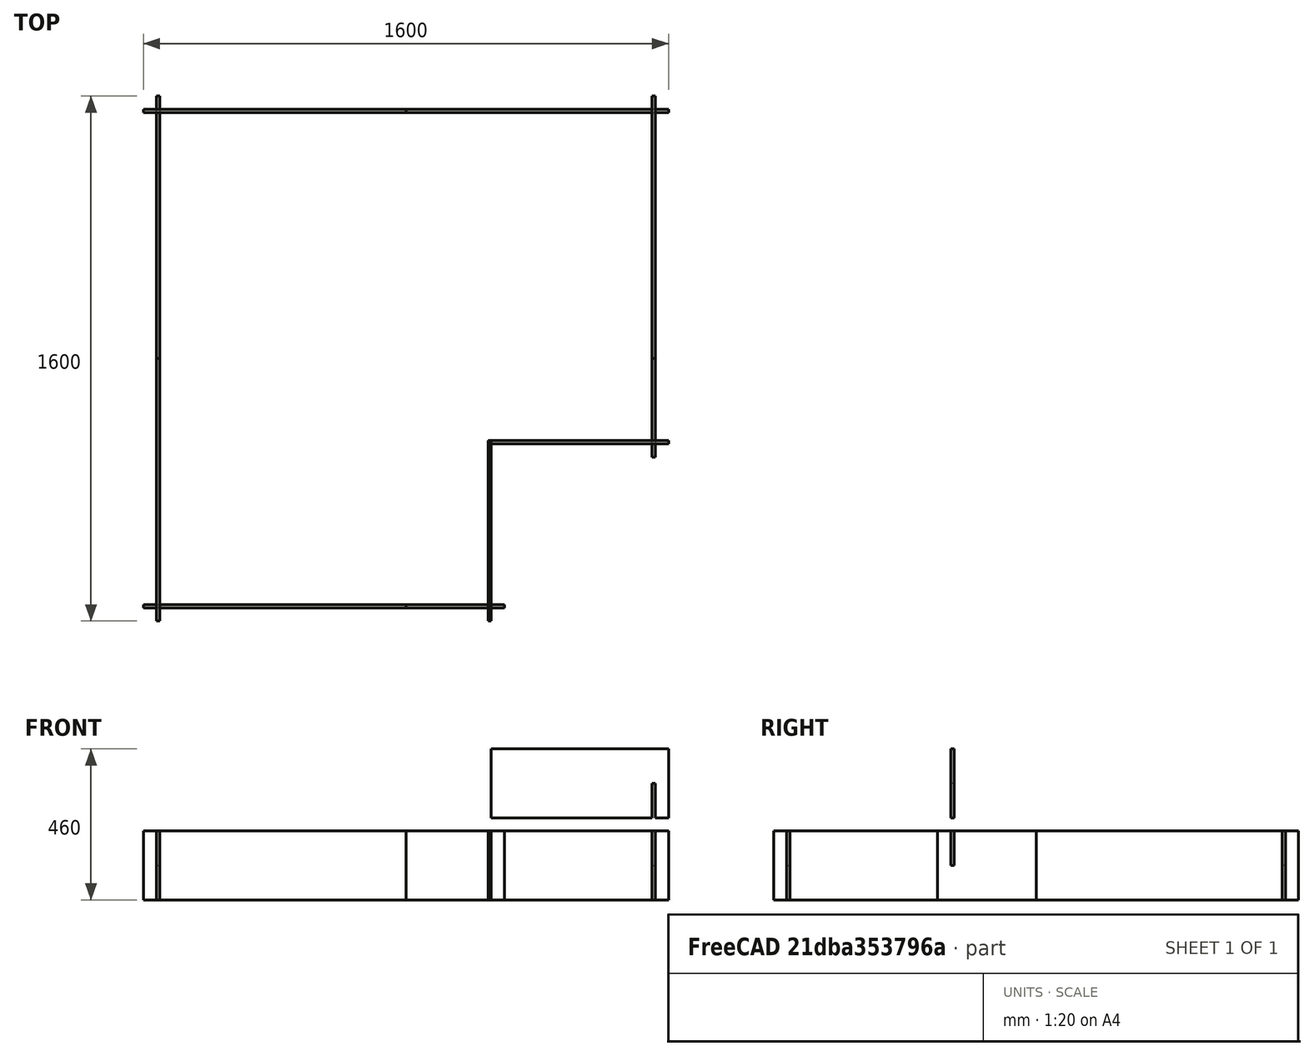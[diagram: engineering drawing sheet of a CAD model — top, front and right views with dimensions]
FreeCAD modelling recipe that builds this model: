
FCSTD DOCUMENT  (FreeCAD 0.21R30769 (Git))
Label: simpler-arena
License: All rights reserved
LicenseURL: http://en.wikipedia.org/wiki/All_rights_reserved
objects: TechDraw::DrawViewAnnotation×14, TechDraw::DrawViewDimension×12, PartDesign::ShapeBinder×11, PartDesign::Body×11, PartDesign::Pad×10, PartDesign::Pocket×10, PartDesign::SubShapeBinder×9, Sketcher::SketchObject×6, TechDraw::DrawViewPart×6, TechDraw::DrawHatch×5, TechDraw::DrawSVGTemplate×3, TechDraw::DrawPage×3, Spreadsheet::Sheet×2, App::Part×2, TechDraw::DrawLeaderLine×1
note: 77 computed .brp shape members not serialized (recipe doc carries the construction recipe); baked Part::Feature solids carry a one-line shape summary decoded from their .brp

FEATURE [Sketcher::SketchObject] Sketch  label="MainSketch"
  FullyConstrained = true
  MapMode = 5
  Support = -> [XY_Plane001]
  expr: Constraints[13] = Spreadsheet.arena_cutout_width
  expr: Constraints[14] = Spreadsheet.arena_inner_width
  expr: Constraints[15] = Spreadsheet.arena_inner_height
  expr: Constraints[16] = Spreadsheet.arena_cutout_height
  sketch-geometry (6):
    g0: LineSegment StartX=-750 StartY=750 StartZ=0 EndX=750 EndY=750 EndZ=0
    g1: LineSegment StartX=750 StartY=750 StartZ=0 EndX=750 EndY=-250 EndZ=0
    g2: LineSegment StartX=250 StartY=-750 StartZ=0 EndX=-750 EndY=-750 EndZ=0
    g3: LineSegment StartX=-750 StartY=-750 StartZ=0 EndX=-750 EndY=750 EndZ=0
    g4: LineSegment StartX=250 StartY=-750 StartZ=0 EndX=250 EndY=-250 EndZ=0
    g5: LineSegment StartX=250 StartY=-250 StartZ=0 EndX=750 EndY=-250 EndZ=0
  constraints (17):
    c: Coincident(g0,g1)
    c: Coincident(g2,g3)
    c: Coincident(g3,g0)
    c: Horizontal(g0)
    c: Horizontal(g2)
    c: Vertical(g1)
    c: Vertical(g3)
    c: Vertical(g4)
    c: Coincident(g5,g4)
    c: Horizontal(g5)
    c: Coincident(g1,g5)
    c: Coincident(g2,g4)
    c: Symmetric(g0,g2,g-1)
    c: DistanceX(g5,g5) = 500
    c: DistanceX(g0,g0) = 1500
    c: DistanceY(g3,g3) = 1500
    c: DistanceY(g4,g4) = 500
FEATURE [Sketcher::SketchObject] Sketch001  label="WallSketch"
  ExternalGeometry = -> [Sketch]
  FullyConstrained = true
  MapMode = 5
  Support = -> [XY_Plane001]
  expr: .Constraints.tab = Spreadsheet.tab_length
  expr: Constraints[101] = Spreadsheet.tab_length
  expr: Constraints[102] = Spreadsheet.tab_length
  expr: Constraints[103] = Spreadsheet.tab_length
  expr: Constraints[109] = Spreadsheet.tab_length
  expr: Constraints[91] = Spreadsheet.wall_thickness
  sketch-geometry (40):
    g0: LineSegment StartX=-750 StartY=0 StartZ=0 EndX=-760 EndY=0 EndZ=0
    g1: LineSegment StartX=-760 StartY=0 StartZ=0 EndX=-760 EndY=800 EndZ=0
    g2: LineSegment StartX=-760 StartY=800 StartZ=0 EndX=-750 EndY=800 EndZ=0
    g3: LineSegment StartX=-750 StartY=800 StartZ=0 EndX=-750 EndY=0 EndZ=0
    g4: LineSegment StartX=-750 StartY=0 StartZ=0 EndX=-760 EndY=0 EndZ=0
    g5: LineSegment StartX=-760 StartY=0 StartZ=0 EndX=-760 EndY=-800 EndZ=0
    g6: LineSegment StartX=-760 StartY=-800 StartZ=0 EndX=-750 EndY=-800 EndZ=0
    g7: LineSegment StartX=-750 StartY=-800 StartZ=0 EndX=-750 EndY=0 EndZ=0
    g8: LineSegment StartX=0 StartY=-750 StartZ=0 EndX=-800 EndY=-750 EndZ=0
    g9: LineSegment StartX=-800 StartY=-750 StartZ=0 EndX=-800 EndY=-760 EndZ=0
    g10: LineSegment StartX=-800 StartY=-760 StartZ=0 EndX=0 EndY=-760 EndZ=0
    g11: LineSegment StartX=0 StartY=-760 StartZ=0 EndX=0 EndY=-750 EndZ=0
    g12: LineSegment StartX=0 StartY=-750 StartZ=0 EndX=300 EndY=-750 EndZ=0
    g13: LineSegment StartX=300 StartY=-750 StartZ=0 EndX=300 EndY=-760 EndZ=0
    g14: LineSegment StartX=300 StartY=-760 StartZ=0 EndX=0 EndY=-760 EndZ=0
    g15: LineSegment StartX=0 StartY=-760 StartZ=0 EndX=0 EndY=-750 EndZ=0
    g16: LineSegment StartX=250 StartY=-250 StartZ=0 EndX=260 EndY=-250 EndZ=0
    g17: LineSegment StartX=260 StartY=-250 StartZ=0 EndX=260 EndY=-800 EndZ=0
    g18: LineSegment StartX=260 StartY=-800 StartZ=0 EndX=250 EndY=-800 EndZ=0
    g19: LineSegment StartX=250 StartY=-800 StartZ=0 EndX=250 EndY=-250 EndZ=0
    g20: LineSegment StartX=260 StartY=-250 StartZ=0 EndX=800 EndY=-250 EndZ=0
    g21: LineSegment StartX=800 StartY=-250 StartZ=0 EndX=800 EndY=-260 EndZ=0
    g22: LineSegment StartX=800 StartY=-260 StartZ=0 EndX=260 EndY=-260 EndZ=0
    g23: LineSegment StartX=260 StartY=-260 StartZ=0 EndX=260 EndY=-250 EndZ=0
    g24: LineSegment StartX=750 StartY=0 StartZ=0 EndX=760 EndY=0 EndZ=0
    g25: LineSegment StartX=760 StartY=0 StartZ=0 EndX=760 EndY=-300 EndZ=0
    g26: LineSegment StartX=760 StartY=-300 StartZ=0 EndX=750 EndY=-300 EndZ=0
    g27: LineSegment StartX=750 StartY=-300 StartZ=0 EndX=750 EndY=0 EndZ=0
    g28: LineSegment StartX=750 StartY=0 StartZ=0 EndX=760 EndY=0 EndZ=0
    g29: LineSegment StartX=760 StartY=0 StartZ=0 EndX=760 EndY=800 EndZ=0
    g30: LineSegment StartX=760 StartY=800 StartZ=0 EndX=750 EndY=800 EndZ=0
    g31: LineSegment StartX=750 StartY=800 StartZ=0 EndX=750 EndY=0 EndZ=0
    g32: LineSegment StartX=0 StartY=750 StartZ=0 EndX=800 EndY=750 EndZ=0
    g33: LineSegment StartX=800 StartY=750 StartZ=0 EndX=800 EndY=760 EndZ=0
    g34: LineSegment StartX=800 StartY=760 StartZ=0 EndX=0 EndY=760 EndZ=0
    g35: LineSegment StartX=0 StartY=760 StartZ=0 EndX=0 EndY=750 EndZ=0
    g36: LineSegment StartX=0 StartY=750 StartZ=0 EndX=-800 EndY=750 EndZ=0
    g37: LineSegment StartX=-800 StartY=750 StartZ=0 EndX=-800 EndY=760 EndZ=0
    g38: LineSegment StartX=-800 StartY=760 StartZ=0 EndX=0 EndY=760 EndZ=0
    g39: LineSegment StartX=0 StartY=760 StartZ=0 EndX=0 EndY=750 EndZ=0
  constraints (114):
    c: Coincident(g0,g1)
    c: Coincident(g1,g2)
    c: Coincident(g2,g3)
    c: Coincident(g3,g0)
    c: Horizontal(g0)
    c: Horizontal(g2)
    c: Vertical(g1)
    c: Vertical(g3)
    c: PointOnObject(g0,g-4)
    c: Coincident(g4,g5)
    c: Coincident(g5,g6)
    c: Coincident(g6,g7)
    c: Coincident(g7,g4)
    c: Horizontal(g4)
    c: Horizontal(g6)
    c: Vertical(g5)
    c: Vertical(g7)
    c: PointOnObject(g4,g-4)
    c: Coincident(g8,g9)
    c: Coincident(g9,g10)
    c: Coincident(g10,g11)
    c: Coincident(g11,g8)
    c: Horizontal(g8)
    c: Horizontal(g10)
    c: Vertical(g9)
    c: Vertical(g11)
    c: PointOnObject(g8,g-5)
    c: Coincident(g12,g13)
    c: Coincident(g13,g14)
    c: Coincident(g14,g15)
    c: Coincident(g15,g12)
    c: Horizontal(g12)
    c: Horizontal(g14)
    c: Vertical(g13)
    c: Vertical(g15)
    c: Coincident(g16,g17)
    c: Coincident(g17,g18)
    c: Coincident(g18,g19)
    c: Coincident(g19,g16)
    c: Horizontal(g18)
    c: Vertical(g17)
    c: Vertical(g19)
    c: Coincident(g20,g21)
    c: Coincident(g21,g22)
    c: Coincident(g22,g23)
    c: Coincident(g23,g20)
    c: Horizontal(g20)
    c: Horizontal(g22)
    c: Vertical(g21)
    c: Coincident(g24,g25)
    c: Coincident(g25,g26)
    c: Coincident(g26,g27)
    c: Coincident(g27,g24)
    c: Horizontal(g24)
    c: Horizontal(g26)
    c: Vertical(g25)
    c: Vertical(g27)
    c: PointOnObject(g24,g-8)
    c: Coincident(g28,g29)
    c: Coincident(g29,g30)
    c: Coincident(g30,g31)
    c: Coincident(g31,g28)
    c: Horizontal(g28)
    c: Horizontal(g30)
    c: Vertical(g29)
    c: Vertical(g31)
    c: PointOnObject(g28,g-8)
    c: Coincident(g32,g33)
    c: Coincident(g33,g34)
    c: Coincident(g34,g35)
    c: Coincident(g35,g32)
    c: Horizontal(g32)
    c: Horizontal(g34)
    c: Vertical(g33)
    c: Vertical(g35)
    c: PointOnObject(g32,g-3)
    c: Coincident(g36,g37)
    c: Coincident(g37,g38)
    c: Coincident(g38,g39)
    c: Coincident(g39,g36)
    c: Horizontal(g36)
    c: Horizontal(g38)
    c: Vertical(g37)
    c: Vertical(g39)
    c: PointOnObject(g36,g-3)
    c: Equal(g37,g2)
    c: Equal(g9,g6)
    c: Equal(g11,g15)
    c: Equal(g13,g18)
    c: Equal(g21,g26)
    c: Equal(g33,g30)
    c: DistanceX(g26,g26) = 10
    c: PointOnObject(g8,g-2)
    c: Coincident(g8,g12)
    c: PointOnObject(g4,g-1)
    c: Coincident(g0,g4)
    c: PointOnObject(g38,g-2)
    c: Coincident(g34,g38)
    c: PointOnObject(g24,g-1)
    c: Coincident(g28,g24)
    c: DistanceX(g-8,g20) = 50  'tab'
    c: DistanceY(g26,g-8) = 50
    c: DistanceX(g-6,g12) = 50
    c: DistanceX(g8,g-5) = 50
    c: Equal(g8,g7)
    c: Equal(g7,g3)
    c: Equal(g3,g36)
    c: Equal(g36,g32)
    c: Equal(g32,g31)
    c: DistanceY(g18,g-6) = 50
    c: Coincident(g16,g-7)
    c: PointOnObject(g20,g-7)
    c: Coincident(g16,g20)
    c: Vertical(g23)
FEATURE [Spreadsheet::Sheet] Spreadsheet
  cells = A1=A2 Height; B1(a2_height)=420; C1=All units mm; A2=Wall Height; B2(wall_height)==a2_height / 2; A3=Wall thickness; B3(wall_thickness)=10; A4=Tab extension; B4(tab_extension)=40; C4=past the intersection; A5=arena inner width; B5(arena_inner_width)=1500; A6=arena inner height; B6(arena_inner_height)=1500; A7=arena cutout width; B7(arena_cutout_width)=500; A8=arena cutout height; B8(arena_cutout_height)=500; A9=tab length; B9(tab_length)==tab_extension + wall_thickness; A10=A2 Width; B10(a2_width)=594
FEATURE [Sketcher::SketchObject] Sketch002  label="CutOuts"
  ExternalGeometry = -> [Sketch001,Sketch]
  FullyConstrained = true
  MapMode = 5
  Support = -> [XY_Plane001]
  sketch-geometry (20):
    g0: LineSegment StartX=-760 StartY=-750 StartZ=0 EndX=-750 EndY=-750 EndZ=0
    g1: LineSegment StartX=-750 StartY=-750 StartZ=0 EndX=-750 EndY=-760 EndZ=0
    g2: LineSegment StartX=-750 StartY=-760 StartZ=0 EndX=-760 EndY=-760 EndZ=0
    g3: LineSegment StartX=-760 StartY=-760 StartZ=0 EndX=-760 EndY=-750 EndZ=0
    g4: LineSegment StartX=250 StartY=-750 StartZ=0 EndX=260 EndY=-750 EndZ=0
    g5: LineSegment StartX=260 StartY=-750 StartZ=0 EndX=260 EndY=-760 EndZ=0
    g6: LineSegment StartX=260 StartY=-760 StartZ=0 EndX=250 EndY=-760 EndZ=0
    g7: LineSegment StartX=250 StartY=-760 StartZ=0 EndX=250 EndY=-750 EndZ=0
    g8: LineSegment StartX=750 StartY=-250 StartZ=0 EndX=760 EndY=-250 EndZ=0
    g9: LineSegment StartX=760 StartY=-250 StartZ=0 EndX=760 EndY=-260 EndZ=0
    g10: LineSegment StartX=760 StartY=-260 StartZ=0 EndX=750 EndY=-260 EndZ=0
    g11: LineSegment StartX=750 StartY=-260 StartZ=0 EndX=750 EndY=-250 EndZ=0
    g12: LineSegment StartX=750 StartY=750 StartZ=0 EndX=760 EndY=750 EndZ=0
    g13: LineSegment StartX=760 StartY=750 StartZ=0 EndX=760 EndY=760 EndZ=0
    g14: LineSegment StartX=760 StartY=760 StartZ=0 EndX=750 EndY=760 EndZ=0
    g15: LineSegment StartX=750 StartY=760 StartZ=0 EndX=750 EndY=750 EndZ=0
    g16: LineSegment StartX=-750 StartY=750 StartZ=0 EndX=-760 EndY=750 EndZ=0
    g17: LineSegment StartX=-760 StartY=750 StartZ=0 EndX=-760 EndY=760 EndZ=0
    g18: LineSegment StartX=-760 StartY=760 StartZ=0 EndX=-750 EndY=760 EndZ=0
    g19: LineSegment StartX=-750 StartY=760 StartZ=0 EndX=-750 EndY=750 EndZ=0
  constraints (58):
    c: Coincident(g0,g1)
    c: Coincident(g1,g2)
    c: Coincident(g2,g3)
    c: Coincident(g3,g0)
    c: Horizontal(g0)
    c: Horizontal(g2)
    c: Vertical(g1)
    c: Vertical(g3)
    c: PointOnObject(g0,g-22)
    c: PointOnObject(g1,g-20)
    c: PointOnObject(g0,g-21)
    c: PointOnObject(g1,g-23)
    c: Coincident(g4,g5)
    c: Coincident(g5,g6)
    c: Coincident(g6,g7)
    c: Coincident(g7,g4)
    c: Horizontal(g4)
    c: Horizontal(g6)
    c: Vertical(g5)
    c: Vertical(g7)
    c: Coincident(g8,g9)
    c: Coincident(g9,g10)
    c: Coincident(g10,g11)
    c: Coincident(g11,g8)
    c: Horizontal(g8)
    c: Vertical(g9)
    c: Vertical(g11)
    c: Coincident(g8,g-11)
    c: Coincident(g12,g13)
    c: Coincident(g13,g14)
    c: Coincident(g14,g15)
    c: Coincident(g15,g12)
    c: Horizontal(g12)
    c: Horizontal(g14)
    c: Vertical(g13)
    c: Vertical(g15)
    c: Coincident(g12,g-11)
    c: PointOnObject(g13,g-10)
    c: PointOnObject(g13,g-9)
    c: Coincident(g16,g17)
    c: Coincident(g17,g18)
    c: Coincident(g18,g19)
    c: Coincident(g19,g16)
    c: Horizontal(g16)
    c: Horizontal(g18)
    c: Vertical(g17)
    c: Vertical(g19)
    c: PointOnObject(g16,g-3)
    c: PointOnObject(g17,g-6)
    c: PointOnObject(g17,g-5)
    c: PointOnObject(g16,g-4)
    c: PointOnObject(g8,g-13)
    c: PointOnObject(g9,g-16)
    c: PointOnObject(g10,g-16)
    c: PointOnObject(g6,g-24)
    c: PointOnObject(g4,g-18)
    c: PointOnObject(g4,g-25)
    c: PointOnObject(g6,g-19)
FEATURE [PartDesign::ShapeBinder] ShapeBinder
  Support = -> [Sketch001]
  TraceSupport = false
FEATURE [PartDesign::Pad] Pad
  Direction = (0,0,1)
  Length = 210
  Length2 = 10
  Profile = -> ShapeBinder
  Type = 0
  expr: Length = Spreadsheet.wall_height
FEATURE [PartDesign::ShapeBinder] ShapeBinder001
  Support = -> [Sketch002]
  TraceSupport = false
FEATURE [PartDesign::Pocket] Pocket
  BaseFeature = -> Pad
  Direction = (0,0,-1)
  Length = 105
  Length2 = 5
  Profile = -> ShapeBinder001
  Reversed = true
  Type = 0
  expr: Length = Spreadsheet.wall_height / 2
FEATURE [PartDesign::Body] Body001  label="Wall1_A"
  Group = -> [ShapeBinder,Pad,ShapeBinder001,Pocket]
  Origin = -> Origin002
  Tip = -> Pocket
FEATURE [PartDesign::ShapeBinder] ShapeBinder002
  Support = -> [Sketch001]
  TraceSupport = false
FEATURE [PartDesign::Pad] Pad001
  Direction = (0,0,1)
  Length = 210
  Length2 = 10
  Profile = -> ShapeBinder002
  Type = 0
  expr: Length = Spreadsheet.wall_height
FEATURE [PartDesign::SubShapeBinder] Binder
  BindCopyOnChange = 0
  BindMode = 0
  ClaimChildren = false
  Context = -> Part011 [Body002.Binder.]
  Fuse = false
  MakeFace = true
  OffsetFill = false
  OffsetIntersection = false
  OffsetJoinType = 0
  OffsetOpenResult = false
  PartialLoad = false
  Placement = pos=(0,0,210) rot=(0,0,1;0rad)
  Relative = true
  Support = -> [Part[Body.Sketch002.Edge20,Body.Sketch002.Edge19,Body.Sketch002.Edge18,Body.Sketch002.Edge17]]
  _Version = 2
  expr: .Placement.Base.z = Spreadsheet.wall_height
FEATURE [PartDesign::Pocket] Pocket001
  BaseFeature = -> Pad001
  Direction = (0,0,-1)
  Length = 105
  Length2 = 5
  Profile = -> Binder
  Type = 0
  expr: Length = Spreadsheet.wall_height / 2
FEATURE [PartDesign::Body] Body002  label="Wall2_A"
  Group = -> [ShapeBinder002,Pad001,Binder,Pocket001]
  Origin = -> Origin003
  Tip = -> Pocket001
FEATURE [PartDesign::ShapeBinder] ShapeBinder003
  Support = -> [Sketch001]
  TraceSupport = false
FEATURE [PartDesign::Pad] Pad002
  Direction = (0,0,1)
  Length = 210
  Length2 = 10
  Profile = -> ShapeBinder003
  Type = 0
  expr: Length = Spreadsheet.wall_height
FEATURE [PartDesign::SubShapeBinder] Binder001
  BindCopyOnChange = 0
  BindMode = 0
  ClaimChildren = false
  Context = -> Part011 [Body003.Binder001.]
  Fuse = false
  MakeFace = true
  OffsetFill = false
  OffsetIntersection = false
  OffsetJoinType = 0
  OffsetOpenResult = false
  PartialLoad = false
  Placement = pos=(0,0,210) rot=(0,0,1;0rad)
  Relative = true
  Support = -> [Part[Body.Sketch002.Edge8,Body.Sketch002.Edge5,Body.Sketch002.Edge6,Body.Sketch002.Edge7]]
  _Version = 2
  expr: .Placement.Base.z = Spreadsheet.wall_height
FEATURE [PartDesign::Pocket] Pocket002
  BaseFeature = -> Pad002
  Direction = (0,0,-1)
  Length = 105
  Length2 = 5
  Profile = -> Binder001
  Type = 0
  expr: Length = Spreadsheet.wall_height / 2
FEATURE [PartDesign::Body] Body003  label="Body003_B"
  Group = -> [ShapeBinder003,Pad002,Binder001,Pocket002]
  Origin = -> Origin007
  Tip = -> Pocket002
FEATURE [PartDesign::ShapeBinder] ShapeBinder005
  Support = -> [Sketch001]
  TraceSupport = false
FEATURE [PartDesign::Pad] Pad003
  Direction = (0,0,1)
  Length = 210
  Length2 = 10
  Profile = -> ShapeBinder005
  Type = 0
  expr: Length = Spreadsheet.wall_height
FEATURE [PartDesign::SubShapeBinder] Binder002
  BindCopyOnChange = 0
  BindMode = 0
  ClaimChildren = false
  Context = -> Part011 [Body004.Binder002.]
  Fuse = false
  MakeFace = true
  OffsetFill = false
  OffsetIntersection = false
  OffsetJoinType = 0
  OffsetOpenResult = false
  PartialLoad = false
  Relative = true
  Support = -> [Part[Body.Sketch002.Edge8,Body.Sketch002.Edge5,Body.Sketch002.Edge6,Body.Sketch002.Edge7]]
  _Version = 2
FEATURE [PartDesign::Pocket] Pocket003
  BaseFeature = -> Pad003
  Direction = (0,0,-1)
  Length = 105
  Length2 = 5
  Profile = -> Binder002
  Reversed = true
  Type = 0
  expr: Length = Spreadsheet.wall_height / 2
FEATURE [PartDesign::Body] Body004  label="Body004_C"
  Group = -> [ShapeBinder005,Pad003,Binder002,Pocket003]
  Origin = -> Origin009
  Tip = -> Pocket003
FEATURE [PartDesign::ShapeBinder] ShapeBinder006
  Support = -> [Sketch001]
  TraceSupport = false
FEATURE [PartDesign::Pad] Pad004
  Direction = (0,0,1)
  Length = 210
  Length2 = 10
  Profile = -> ShapeBinder006
  Type = 0
  expr: Length = Spreadsheet.wall_height
FEATURE [PartDesign::SubShapeBinder] Binder003
  BindCopyOnChange = 0
  BindMode = 0
  ClaimChildren = false
  Context = -> Part011 [Body005.Binder003.]
  Fuse = false
  MakeFace = true
  OffsetFill = false
  OffsetIntersection = false
  OffsetJoinType = 0
  OffsetOpenResult = false
  PartialLoad = false
  Placement = pos=(0,0,250) rot=(0,0,1;0rad)
  Relative = true
  Support = -> [Part[Body.Sketch002.Edge12,Body.Sketch002.Edge9,Body.Sketch002.Edge10,Body.Sketch002.Edge11]]
  _Version = 2
FEATURE [PartDesign::Pocket] Pocket004
  BaseFeature = -> Pad004
  Direction = (0,0,-1)
  Length = 105
  Length2 = 5
  Profile = -> Binder003
  Reversed = true
  Type = 0
  expr: Length = Spreadsheet.wall_height / 2
FEATURE [PartDesign::Body] Body005  label="Body005_D"
  Group = -> [ShapeBinder006,Pad004,Binder003,Pocket004]
  Origin = -> Origin011
  Placement = pos=(0,0,250) rot=(0,0,1;0rad)
  Tip = -> Pocket004
FEATURE [PartDesign::ShapeBinder] ShapeBinder007
  Support = -> [Sketch001]
  TraceSupport = false
FEATURE [PartDesign::Pad] Pad005
  Direction = (0,0,1)
  Length = 210
  Length2 = 10
  Profile = -> ShapeBinder007
  Type = 0
  expr: Length = Spreadsheet.wall_height
FEATURE [PartDesign::SubShapeBinder] Binder004
  BindCopyOnChange = 0
  BindMode = 0
  ClaimChildren = false
  Context = -> Part011 [Body006.Binder004.]
  Fuse = false
  MakeFace = true
  OffsetFill = false
  OffsetIntersection = false
  OffsetJoinType = 0
  OffsetOpenResult = false
  PartialLoad = false
  Placement = pos=(0,0,210) rot=(0,0,1;0rad)
  Relative = true
  Support = -> [Part[Body.Sketch002.Edge12,Body.Sketch002.Edge9,Body.Sketch002.Edge10,Body.Sketch002.Edge11]]
  _Version = 2
  expr: .Placement.Base.z = Spreadsheet.wall_height
FEATURE [PartDesign::Pocket] Pocket005
  BaseFeature = -> Pad005
  Direction = (0,0,-1)
  Length = 105
  Length2 = 5
  Profile = -> Binder004
  Type = 0
  expr: Length = Spreadsheet.wall_height / 2
FEATURE [PartDesign::Body] Body006  label="Body006_B"
  Group = -> [ShapeBinder007,Pad005,Binder004,Pocket005]
  Origin = -> Origin013
  Tip = -> Pocket005
FEATURE [PartDesign::ShapeBinder] ShapeBinder008
  Support = -> [Sketch001]
  TraceSupport = false
FEATURE [PartDesign::Pad] Pad006
  Direction = (0,0,1)
  Length = 210
  Length2 = 10
  Profile = -> ShapeBinder008
  Type = 0
  expr: Length = Spreadsheet.wall_height
FEATURE [PartDesign::SubShapeBinder] Binder005
  BindCopyOnChange = 0
  BindMode = 0
  ClaimChildren = false
  Context = -> Part011 [Body007.Binder005.]
  Fuse = false
  MakeFace = true
  OffsetFill = false
  OffsetIntersection = false
  OffsetJoinType = 0
  OffsetOpenResult = false
  PartialLoad = false
  Relative = true
  Support = -> [Part[Body.Sketch002.Edge16,Body.Sketch002.Edge15,Body.Sketch002.Edge14,Body.Sketch002.Edge13]]
  _Version = 2
FEATURE [PartDesign::Pocket] Pocket006
  BaseFeature = -> Pad006
  Direction = (0,0,-1)
  Length = 105
  Length2 = 5
  Profile = -> Binder005
  Reversed = true
  Type = 0
  expr: Length = Spreadsheet.wall_height / 2
FEATURE [PartDesign::Body] Body007  label="Body007_A"
  Group = -> [ShapeBinder008,Pad006,Binder005,Pocket006]
  Origin = -> Origin015
  Tip = -> Pocket006
FEATURE [PartDesign::ShapeBinder] ShapeBinder009
  Support = -> [Sketch001]
  TraceSupport = false
FEATURE [PartDesign::Pad] Pad007
  Direction = (0,0,1)
  Length = 210
  Length2 = 10
  Profile = -> ShapeBinder009
  Type = 0
  expr: Length = Spreadsheet.wall_height
FEATURE [PartDesign::SubShapeBinder] Binder006
  BindCopyOnChange = 0
  BindMode = 0
  ClaimChildren = false
  Context = -> Part011 [Body008.Binder006.]
  Fuse = false
  MakeFace = true
  OffsetFill = false
  OffsetIntersection = false
  OffsetJoinType = 0
  OffsetOpenResult = false
  PartialLoad = false
  Placement = pos=(0,0,210) rot=(0,0,1;0rad)
  Relative = true
  Support = -> [Part[Body.Sketch002.Edge16,Body.Sketch002.Edge15,Body.Sketch002.Edge14,Body.Sketch002.Edge13]]
  _Version = 2
  expr: .Placement.Base.z = Spreadsheet.wall_height
FEATURE [PartDesign::Pocket] Pocket007
  BaseFeature = -> Pad007
  Direction = (0,0,-1)
  Length = 105
  Length2 = 5
  Profile = -> Binder006
  Type = 0
  expr: Length = Spreadsheet.wall_height / 2
FEATURE [PartDesign::Body] Body008  label="Body008_A"
  Group = -> [ShapeBinder009,Pad007,Binder006,Pocket007]
  Origin = -> Origin017
  Tip = -> Pocket007
FEATURE [PartDesign::ShapeBinder] ShapeBinder010
  Support = -> [Sketch001]
  TraceSupport = false
FEATURE [PartDesign::Pad] Pad008
  Direction = (0,0,1)
  Length = 210
  Length2 = 10
  Profile = -> ShapeBinder010
  Type = 0
  expr: Length = Spreadsheet.wall_height
FEATURE [PartDesign::SubShapeBinder] Binder007
  BindCopyOnChange = 0
  BindMode = 0
  ClaimChildren = false
  Context = -> Part011 [Body009.Binder007.]
  Fuse = false
  MakeFace = true
  OffsetFill = false
  OffsetIntersection = false
  OffsetJoinType = 0
  OffsetOpenResult = false
  PartialLoad = false
  Relative = true
  Support = -> [Part[Body.Sketch002.Edge1,Body.Sketch002.Edge2,Body.Sketch002.Edge3,Body.Sketch002.Edge4]]
  _Version = 2
FEATURE [PartDesign::Pocket] Pocket008
  BaseFeature = -> Pad008
  Direction = (0,0,-1)
  Length = 105
  Length2 = 5
  Profile = -> Binder007
  Reversed = true
  Type = 0
  expr: Length = Spreadsheet.wall_height / 2
FEATURE [PartDesign::Body] Body009  label="Body009_A"
  Group = -> [ShapeBinder010,Pad008,Binder007,Pocket008]
  Origin = -> Origin019
  Tip = -> Pocket008
FEATURE [PartDesign::ShapeBinder] ShapeBinder011
  Support = -> [Sketch001]
  TraceSupport = false
FEATURE [PartDesign::Pad] Pad009
  Direction = (0,0,1)
  Length = 210
  Length2 = 10
  Profile = -> ShapeBinder011
  Type = 0
  expr: Length = Spreadsheet.wall_height
FEATURE [PartDesign::SubShapeBinder] Binder008
  BindCopyOnChange = 0
  BindMode = 0
  ClaimChildren = false
  Context = -> Part011 [Body010.Binder008.]
  Fuse = false
  MakeFace = true
  OffsetFill = false
  OffsetIntersection = false
  OffsetJoinType = 0
  OffsetOpenResult = false
  PartialLoad = false
  Placement = pos=(0,0,210) rot=(0,0,1;0rad)
  Relative = true
  Support = -> [Part[Body.Sketch002.Edge1,Body.Sketch002.Edge2,Body.Sketch002.Edge4,Body.Sketch002.Edge3]]
  _Version = 2
  expr: .Placement.Base.z = Spreadsheet.wall_height
FEATURE [PartDesign::Pocket] Pocket009
  BaseFeature = -> Pad009
  Direction = (0,0,-1)
  Length = 105
  Length2 = 5
  Profile = -> Binder008
  Type = 0
  expr: Length = Spreadsheet.wall_height / 2
FEATURE [PartDesign::Body] Body010  label="Body010_A"
  Group = -> [ShapeBinder011,Pad009,Binder008,Pocket009]
  Origin = -> Origin021
  Tip = -> Pocket009
FEATURE [Sketcher::SketchObject] Sketch003  label="BaseSketch"
  ExternalGeometry = -> [Sketch,Sketch001]
  FullyConstrained = true
  MapMode = 5
  Support = -> [XY_Plane001]
  expr: Constraints[10] = Spreadsheet.a2_width
  expr: Constraints[11] = Spreadsheet.a2_height
  sketch-geometry (46):
    g0: LineSegment StartX=-800 StartY=800 StartZ=0 EndX=-206 EndY=800 EndZ=0
    g1: LineSegment StartX=-206 StartY=800 StartZ=0 EndX=-206 EndY=380 EndZ=0
    g2: LineSegment StartX=-206 StartY=380 StartZ=0 EndX=-800 EndY=380 EndZ=0
    g3: LineSegment StartX=-800 StartY=380 StartZ=0 EndX=-800 EndY=800 EndZ=0
    g4: LineSegment StartX=-800 StartY=380 StartZ=0 EndX=-206 EndY=380 EndZ=0
    g5: LineSegment StartX=-206 StartY=380 StartZ=0 EndX=-206 EndY=-40 EndZ=0
    g6: LineSegment StartX=-206 StartY=-40 StartZ=0 EndX=-800 EndY=-40 EndZ=0
    g7: LineSegment StartX=-800 StartY=-40 StartZ=0 EndX=-800 EndY=380 EndZ=0
    g8: LineSegment StartX=-800 StartY=-40 StartZ=0 EndX=-206 EndY=-40 EndZ=0
    g9: LineSegment StartX=-206 StartY=-40 StartZ=0 EndX=-206 EndY=-460 EndZ=0
    g10: LineSegment StartX=-206 StartY=-460 StartZ=0 EndX=-800 EndY=-460 EndZ=0
    g11: LineSegment StartX=-800 StartY=-460 StartZ=0 EndX=-800 EndY=-40 EndZ=0
    g12: LineSegment StartX=-800 StartY=-460 StartZ=0 EndX=-206 EndY=-460 EndZ=0
    g13: LineSegment StartX=-206 StartY=-460 StartZ=0 EndX=-206 EndY=-800 EndZ=0
    g14: LineSegment StartX=-206 StartY=-800 StartZ=0 EndX=-800 EndY=-800 EndZ=0
    g15: LineSegment StartX=-800 StartY=-800 StartZ=0 EndX=-800 EndY=-460 EndZ=0
    g16: LineSegment StartX=-206 StartY=800 StartZ=0 EndX=388 EndY=800 EndZ=0
    g17: LineSegment StartX=388 StartY=800 StartZ=0 EndX=388 EndY=380 EndZ=0
    g18: LineSegment StartX=388 StartY=380 StartZ=0 EndX=-206 EndY=380 EndZ=0
    g19: LineSegment StartX=-206 StartY=380 StartZ=0 EndX=-206 EndY=800 EndZ=0
    g20: LineSegment StartX=-206 StartY=380 StartZ=0 EndX=388 EndY=380 EndZ=0
    g21: LineSegment StartX=388 StartY=380 StartZ=0 EndX=388 EndY=-40 EndZ=0
    g22: LineSegment StartX=388 StartY=-40 StartZ=0 EndX=-206 EndY=-40 EndZ=0
    g23: LineSegment StartX=-206 StartY=-40 StartZ=0 EndX=-206 EndY=380 EndZ=0
    g24: LineSegment StartX=-206 StartY=-40 StartZ=0 EndX=388 EndY=-40 EndZ=0
    g25: LineSegment StartX=-206 StartY=-460 StartZ=0 EndX=-206 EndY=-40 EndZ=0
    g26: LineSegment StartX=-206 StartY=-460 StartZ=0 EndX=300 EndY=-460 EndZ=0
    g27: LineSegment StartX=300 StartY=-460 StartZ=0 EndX=300 EndY=-800 EndZ=0
    g28: LineSegment StartX=300 StartY=-800 StartZ=0 EndX=-206 EndY=-800 EndZ=0
    g29: LineSegment StartX=-206 StartY=-800 StartZ=0 EndX=-206 EndY=-460 EndZ=0
    g30: LineSegment StartX=388 StartY=800 StartZ=0 EndX=800 EndY=800 EndZ=0
    g31: LineSegment StartX=800 StartY=800 StartZ=0 EndX=800 EndY=380 EndZ=0
    g32: LineSegment StartX=800 StartY=380 StartZ=0 EndX=388 EndY=380 EndZ=0
    g33: LineSegment StartX=388 StartY=380 StartZ=0 EndX=388 EndY=800 EndZ=0
    g34: LineSegment StartX=388 StartY=380 StartZ=0 EndX=800 EndY=380 EndZ=0
    g35: LineSegment StartX=800 StartY=380 StartZ=0 EndX=800 EndY=-40 EndZ=0
    g36: LineSegment StartX=800 StartY=-40 StartZ=0 EndX=388 EndY=-40 EndZ=0
    g37: LineSegment StartX=388 StartY=-40 StartZ=0 EndX=388 EndY=380 EndZ=0
    g38: LineSegment StartX=388 StartY=-40 StartZ=0 EndX=800 EndY=-40 EndZ=0
    g39: LineSegment StartX=800 StartY=-40 StartZ=0 EndX=800 EndY=-300 EndZ=0
    g40: LineSegment StartX=800 StartY=-300 StartZ=0 EndX=388 EndY=-300 EndZ=0
    g41: LineSegment StartX=388 StartY=-300 StartZ=0 EndX=388 EndY=-40 EndZ=0
    g42: LineSegment StartX=388 StartY=-460 StartZ=0 EndX=300 EndY=-460 EndZ=0
    g43: LineSegment StartX=300 StartY=-460 StartZ=0 EndX=-206 EndY=-460 EndZ=0
    g44: LineSegment StartX=388 StartY=-40 StartZ=0 EndX=388 EndY=-300 EndZ=0
    g45: LineSegment StartX=388 StartY=-300 StartZ=0 EndX=388 EndY=-460 EndZ=0
  constraints (121):
    c: Coincident(g0,g1)
    c: Coincident(g1,g2)
    c: Coincident(g2,g3)
    c: Coincident(g3,g0)
    c: Horizontal(g0)
    c: Horizontal(g2)
    c: Vertical(g1)
    c: Vertical(g3)
    c: PointOnObject(g-9,g0)
    c: PointOnObject(g-10,g3)
    c: DistanceX(g0,g0) = 594
    c: DistanceY(g3,g3) = 420
    c: Coincident(g4,g5)
    c: Coincident(g5,g6)
    c: Coincident(g6,g7)
    c: Coincident(g7,g4)
    c: Horizontal(g4)
    c: Horizontal(g6)
    c: Vertical(g5)
    c: Vertical(g7)
    c: Coincident(g4,g2)
    c: Equal(g5,g1)
    c: Equal(g2,g6)
    c: Coincident(g8,g9)
    c: Coincident(g9,g10)
    c: Coincident(g10,g11)
    c: Coincident(g11,g8)
    c: Horizontal(g8)
    c: Horizontal(g10)
    c: Vertical(g9)
    c: Vertical(g11)
    c: Coincident(g8,g6)
    c: Equal(g9,g5)
    c: Equal(g10,g6)
    c: Coincident(g12,g13)
    c: Coincident(g13,g14)
    c: Coincident(g14,g15)
    c: Coincident(g15,g12)
    c: Horizontal(g12)
    c: Vertical(g13)
    c: Vertical(g15)
    c: Coincident(g12,g10)
    c: Equal(g14,g10)
    c: Coincident(g16,g17)
    c: Coincident(g17,g18)
    c: Coincident(g18,g19)
    c: Coincident(g19,g16)
    c: Horizontal(g16)
    c: Horizontal(g18)
    c: Vertical(g17)
    c: Vertical(g19)
    c: Coincident(g16,g0)
    c: Equal(g0,g16)
    c: Equal(g17,g1)
    c: Coincident(g20,g21)
    c: Coincident(g21,g22)
    c: Coincident(g22,g23)
    c: Coincident(g23,g20)
    c: Horizontal(g20)
    c: Horizontal(g22)
    c: Vertical(g21)
    c: Vertical(g23)
    c: Coincident(g20,g1)
    c: Equal(g21,g17)
    c: Equal(g22,g6)
    c: Coincident(g24,g44)
    c: Coincident(g45,g42)
    c: Coincident(g43,g25)
    c: Coincident(g25,g24)
    c: Vertical(g25)
    c: Coincident(g24,g5)
    c: Coincident(g26,g27)
    c: Coincident(g27,g28)
    c: Coincident(g28,g29)
    c: Coincident(g29,g26)
    c: Horizontal(g26)
    c: Vertical(g29)
    c: Coincident(g26,g9)
    c: Equal(g27,g13)
    c: Coincident(g30,g31)
    c: Coincident(g31,g32)
    c: Coincident(g32,g33)
    c: Coincident(g33,g30)
    c: Horizontal(g30)
    c: Horizontal(g32)
    c: Vertical(g33)
    c: Coincident(g30,g16)
    c: Equal(g31,g17)
    c: Coincident(g34,g35)
    c: Coincident(g35,g36)
    c: Coincident(g36,g37)
    c: Coincident(g37,g34)
    c: Horizontal(g34)
    c: Horizontal(g36)
    c: Vertical(g35)
    c: Vertical(g37)
    c: Coincident(g34,g17)
    c: Equal(g35,g31)
    c: Equal(g36,g32)
    c: Coincident(g38,g39)
    c: Coincident(g39,g40)
    c: Coincident(g40,g41)
    c: Coincident(g41,g38)
    c: Horizontal(g38)
    c: Vertical(g41)
    c: Coincident(g38,g21)
    c: Equal(g40,g36)
    c: Tangent(g27,g-13)
    c: Coincident(g42,g43)
    c: Horizontal(g43)
    c: Coincident(g42,g26)
    c: Coincident(g24,g21)
    c: Coincident(g44,g45)
    c: Vertical(g45)
    c: Coincident(g40,g44)
    c: Horizontal(g42)
    c: Tangent(g39,g-12)
    c: Vertical(g31)
    c: Tangent(g40,g-14)
    c: Tangent(g-15,g28)
    c: Horizontal(g14)
FEATURE [App::Part] Part011  label="Walls"
  Group = -> [Body001,Body002,Body003,Body004,Body005,Body006,Body007,Body008,Body009,Body010]
  Origin = -> Origin022
FEATURE [TechDraw::DrawSVGTemplate] Template
  Height = 210
  Orientation = 1
  Width = 297
FEATURE [TechDraw::DrawSVGTemplate] Template001
  Height = 210
  Orientation = 1
  Width = 297
FEATURE [Sketcher::SketchObject] Sketch004  label="TargetZoneSketch"
  ExternalGeometry = -> [Sketch001]
  FullyConstrained = true
  MapMode = 5
  Support = -> [XY_Plane001]
  sketch-geometry (4):
    g0: LineSegment StartX=350 StartY=350 StartZ=0 EndX=500 EndY=350 EndZ=0
    g1: LineSegment StartX=500 StartY=350 StartZ=0 EndX=500 EndY=150 EndZ=0
    g2: LineSegment StartX=500 StartY=150 StartZ=0 EndX=350 EndY=150 EndZ=0
    g3: LineSegment StartX=350 StartY=150 StartZ=0 EndX=350 EndY=350 EndZ=0
  constraints (12):
    c: Coincident(g0,g1)
    c: Coincident(g1,g2)
    c: Coincident(g2,g3)
    c: Coincident(g3,g0)
    c: Horizontal(g0)
    c: Horizontal(g2)
    c: Vertical(g1)
    c: Vertical(g3)
    c: DistanceX(g0,g0) = 150
    c: DistanceY(g1,g1) = 200
    c: DistanceX(g0,g-4) = 250
    c: DistanceY(g0,g-3) = 400
FEATURE [TechDraw::DrawSVGTemplate] Template002
  Height = 210
  Orientation = 1
  Width = 297
FEATURE [TechDraw::DrawViewPart] View002
  CoarseView = false
  Direction = (0,-1,0)
  Focus = 100
  HardHidden = false
  IsoCount = 0
  IsoHidden = false
  IsoVisible = false
  LockPosition = false
  Perspective = false
  Rotation = 0
  Scale = 0.25
  ScaleType = 2
  SeamHidden = false
  SeamVisible = true
  SmoothHidden = false
  SmoothVisible = true
  Source = -> [Body010]
  X = 143.594
  XDirection = (1,0,0)
  Y = 163.261
FEATURE [TechDraw::DrawViewPart] View003
  CoarseView = false
  Direction = (0,-1,0)
  Focus = 100
  HardHidden = false
  IsoCount = 0
  IsoHidden = false
  IsoVisible = false
  LockPosition = false
  Perspective = false
  Rotation = 0
  Scale = 0.25
  ScaleType = 2
  SeamHidden = false
  SeamVisible = true
  SmoothHidden = false
  SmoothVisible = true
  Source = -> [Body003]
  X = 54.1654
  XDirection = (1,0,0)
  Y = 98.4454
FEATURE [TechDraw::DrawViewPart] View004
  CoarseView = false
  Direction = (0,-1,0)
  Focus = 100
  HardHidden = false
  IsoCount = 0
  IsoHidden = false
  IsoVisible = false
  LockPosition = false
  Perspective = false
  Rotation = 0
  Scale = 0.25
  ScaleType = 2
  SeamHidden = false
  SeamVisible = true
  SmoothHidden = false
  SmoothVisible = true
  Source = -> [Body005]
  X = 84.0517
  XDirection = (1,0,0)
  Y = 30.0999
FEATURE [TechDraw::DrawViewAnnotation] Annotation
  Font = Lucida Grande
  LineSpace = 80
  LockPosition = false
  MaxWidth = -1
  Rotation = 0
  Scale = 0.1
  ScaleType = 0
  Text = A
  TextSize = 5
  TextStyle = 0
  X = 61.9493
  Y = 98.2891
FEATURE [TechDraw::DrawViewAnnotation] Annotation001
  Font = Lucida Grande
  LineSpace = 80
  LockPosition = false
  MaxWidth = -1
  Rotation = 0
  Scale = 0.1
  ScaleType = 0
  Text = B
  TextSize = 5
  TextStyle = 0
  X = 95.1013
  Y = 79.833
FEATURE [TechDraw::DrawViewAnnotation] Annotation002
  Font = Lucida Grande
  LineSpace = 80
  LockPosition = false
  MaxWidth = -1
  Rotation = 0
  Scale = 0.1
  ScaleType = 0
  Text = C
  TextSize = 5
  TextStyle = 0
  X = 125.734
  Y = 88.9125
FEATURE [TechDraw::DrawViewAnnotation] Annotation003
  Font = Lucida Grande
  LineSpace = 80
  LockPosition = false
  MaxWidth = -1
  Rotation = 0
  Scale = 0.1
  ScaleType = 0
  Text = D
  TextSize = 5
  TextStyle = 0
  X = 157.008
  Y = 106.946
FEATURE [TechDraw::DrawViewAnnotation] Annotation004
  Font = Lucida Grande
  LineSpace = 80
  LockPosition = false
  MaxWidth = -1
  Rotation = 0
  Scale = 0.1
  ScaleType = 0
  Text = B
  TextSize = 5
  TextStyle = 0
  X = 184.814
  Y = 80.4141
FEATURE [TechDraw::DrawViewAnnotation] Annotation005
  Font = Lucida Grande
  LineSpace = 80
  LockPosition = false
  MaxWidth = -1
  Rotation = 0
  Scale = 0.1
  ScaleType = 0
  Text = A
  TextSize = 5
  TextStyle = 0
  X = 224.642
  Y = 104.252
FEATURE [TechDraw::DrawViewAnnotation] Annotation006
  Font = Lucida Grande
  LineSpace = 80
  LockPosition = false
  MaxWidth = -1
  Rotation = 0
  Scale = 0.1
  ScaleType = 0
  Text = A
  TextSize = 5
  TextStyle = 0
  X = 217.312
  Y = 135.217
FEATURE [TechDraw::DrawViewAnnotation] Annotation007
  Font = Lucida Grande
  LineSpace = 80
  LockPosition = false
  MaxWidth = -1
  Rotation = 0
  Scale = 0.1
  ScaleType = 0
  Text = A
  TextSize = 5
  TextStyle = 0
  X = 163.908
  Y = 164.088
FEATURE [TechDraw::DrawViewAnnotation] Annotation008
  Font = Lucida Grande
  LineSpace = 80
  LockPosition = false
  MaxWidth = -1
  Rotation = 0
  Scale = 0.1
  ScaleType = 0
  Text = A
  TextSize = 5
  TextStyle = 0
  X = 117.385
  Y = 165.435
FEATURE [TechDraw::DrawViewAnnotation] Annotation009
  Font = Lucida Grande
  LineSpace = 80
  LockPosition = false
  MaxWidth = -1
  Rotation = 0
  Scale = 0.1
  ScaleType = 0
  Text = A
  TextSize = 5
  TextStyle = 0
  X = 68.6184
  Y = 136.414
FEATURE [TechDraw::DrawViewAnnotation] Annotation010
  Font = Lucida Grande
  LineSpace = 80
  LockPosition = false
  MaxWidth = -1
  Rotation = 0
  ScaleType = 0
  Text = A (x6)
  TextSize = 5
  TextStyle = 0
  X = 139.28
  Y = 167.855
FEATURE [TechDraw::DrawViewAnnotation] Annotation011
  Font = Lucida Grande
  LineSpace = 80
  LockPosition = false
  MaxWidth = -1
  Rotation = 0
  ScaleType = 0
  Text = B (x2)
  TextSize = 5
  TextStyle = 0
  X = 50.9047
  Y = 110
FEATURE [TechDraw::DrawViewDimension] Dimension008
  AngleOverride = false
  Arbitrary = false
  ArbitraryTolerances = false
  EqualTolerance = true
  ExtensionAngle = 0
  FormatSpec = %.2f
  FormatSpecOverTolerance = %+.2f
  FormatSpecUnderTolerance = %+.2f
  Inverted = false
  LineAngle = 0
  LockPosition = false
  MeasureType = 1
  OverTolerance = 0
  References2D = -> [View002]
  Rotation = 0
  ScaleType = 0
  TheoreticalExact = false
  Type = 1
  UnderTolerance = 0
  X = -0.953106
  Y = 42.3822
FEATURE [TechDraw::DrawViewDimension] Dimension011
  AngleOverride = false
  Arbitrary = false
  ArbitraryTolerances = false
  EqualTolerance = true
  ExtensionAngle = 0
  FormatSpec = %.2f
  FormatSpecOverTolerance = %+.2f
  FormatSpecUnderTolerance = %+.2f
  Inverted = false
  LineAngle = 0
  LockPosition = false
  MeasureType = 1
  OverTolerance = 0
  References2D = -> [View002]
  Rotation = 0
  ScaleType = 0
  TheoreticalExact = false
  Type = 2
  UnderTolerance = 0
  X = -109.384
  Y = 11.8858
FEATURE [TechDraw::DrawViewDimension] Dimension012
  AngleOverride = false
  Arbitrary = false
  ArbitraryTolerances = false
  EqualTolerance = true
  ExtensionAngle = 0
  FormatSpec = %.2f
  FormatSpecOverTolerance = %+.2f
  FormatSpecUnderTolerance = %+.2f
  Inverted = false
  LineAngle = 0
  LockPosition = false
  MeasureType = 1
  OverTolerance = 0
  References2D = -> [View002]
  Rotation = 0
  ScaleType = 0
  TheoreticalExact = false
  Type = 2
  UnderTolerance = 0
  X = 106.704
  Y = 0.23493
FEATURE [TechDraw::DrawViewDimension] Dimension009
  AngleOverride = false
  Arbitrary = false
  ArbitraryTolerances = false
  EqualTolerance = true
  ExtensionAngle = 0
  FormatSpec = %.2f
  FormatSpecOverTolerance = %+.2f
  FormatSpecUnderTolerance = %+.2f
  Inverted = false
  LineAngle = 0
  LockPosition = false
  MeasureType = 1
  OverTolerance = 0
  References2D = -> [View002]
  Rotation = 0
  ScaleType = 0
  TheoreticalExact = false
  Type = 1
  UnderTolerance = 0
  X = -90.1542
  Y = 35.275
FEATURE [TechDraw::DrawViewDimension] Dimension010
  AngleOverride = false
  Arbitrary = false
  ArbitraryTolerances = false
  EqualTolerance = true
  ExtensionAngle = 0
  FormatSpec = %.2f
  FormatSpecOverTolerance = %+.2f
  FormatSpecUnderTolerance = %+.2f
  Inverted = false
  LineAngle = 0
  LockPosition = false
  MeasureType = 1
  OverTolerance = 0
  References2D = -> [View002]
  Rotation = 0
  ScaleType = 0
  TheoreticalExact = false
  Type = 1
  UnderTolerance = 0
  X = -59.2878
  Y = 32.7121
FEATURE [TechDraw::DrawViewAnnotation] Annotation012
  Font = Lucida Grande
  LineSpace = 80
  LockPosition = false
  MaxWidth = -1
  Rotation = 0
  ScaleType = 0
  Text = D
  TextSize = 5
  TextStyle = 0
  X = 78.8732
  Y = 36.1999
FEATURE [TechDraw::DrawViewDimension] Dimension017
  AngleOverride = false
  Arbitrary = false
  ArbitraryTolerances = false
  EqualTolerance = true
  ExtensionAngle = 0
  FormatSpec = %.2f
  FormatSpecOverTolerance = %+.2f
  FormatSpecUnderTolerance = %+.2f
  Inverted = false
  LineAngle = 0
  LockPosition = false
  MeasureType = 1
  OverTolerance = 0
  References2D = -> [View004]
  Rotation = 0
  ScaleType = 0
  TheoreticalExact = false
  Type = 1
  UnderTolerance = 0
  X = 0.730795
  Y = 35.2424
FEATURE [TechDraw::DrawViewPart] View005
  CoarseView = false
  Direction = (1,0,0)
  Focus = 100
  HardHidden = false
  IsoCount = 0
  IsoHidden = false
  IsoVisible = false
  LockPosition = false
  Perspective = false
  Rotation = 0
  Scale = 0.25
  ScaleType = 2
  SeamHidden = false
  SeamVisible = true
  SmoothHidden = false
  SmoothVisible = true
  Source = -> [Body004]
  X = 176.136
  XDirection = (0,1,0)
  Y = 98.0999
FEATURE [TechDraw::DrawViewAnnotation] Annotation013
  Font = Lucida Grande
  LineSpace = 80
  LockPosition = false
  MaxWidth = -1
  Rotation = 0
  ScaleType = 0
  Text = C
  TextSize = 5
  TextStyle = 0
  X = 177.983
  Y = 100.823
FEATURE [Sketcher::SketchObject] Sketch005  label="A1BaseSketch"
  ExternalGeometry = -> [Sketch001]
  FullyConstrained = true
  MapMode = 5
  Support = -> [XY_Plane001]
  sketch-geometry (24):
    g0: LineSegment StartX=-800 StartY=800 StartZ=0 EndX=41 EndY=800 EndZ=0
    g1: LineSegment StartX=41 StartY=800 StartZ=0 EndX=41 EndY=206 EndZ=0
    g2: LineSegment StartX=41 StartY=206 StartZ=0 EndX=-800 EndY=206 EndZ=0
    g3: LineSegment StartX=-800 StartY=206 StartZ=0 EndX=-800 EndY=800 EndZ=0
    g4: LineSegment StartX=-800 StartY=206 StartZ=0 EndX=41 EndY=206 EndZ=0
    g5: LineSegment StartX=41 StartY=206 StartZ=0 EndX=41 EndY=-388 EndZ=0
    g6: LineSegment StartX=41 StartY=-388 StartZ=0 EndX=-800 EndY=-388 EndZ=0
    g7: LineSegment StartX=-800 StartY=-388 StartZ=0 EndX=-800 EndY=206 EndZ=0
    g8: LineSegment StartX=-800 StartY=-388 StartZ=0 EndX=41 EndY=-388 EndZ=0
    g9: LineSegment StartX=41 StartY=-388 StartZ=0 EndX=41 EndY=-982 EndZ=0
    g10: LineSegment StartX=41 StartY=-982 StartZ=0 EndX=-800 EndY=-982 EndZ=0
    g11: LineSegment StartX=-800 StartY=-982 StartZ=0 EndX=-800 EndY=-388 EndZ=0
    g12: LineSegment StartX=41 StartY=800 StartZ=0 EndX=882 EndY=800 EndZ=0
    g13: LineSegment StartX=882 StartY=800 StartZ=0 EndX=882 EndY=206 EndZ=0
    g14: LineSegment StartX=882 StartY=206 StartZ=0 EndX=41 EndY=206 EndZ=0
    g15: LineSegment StartX=41 StartY=206 StartZ=0 EndX=41 EndY=800 EndZ=0
    g16: LineSegment StartX=41 StartY=206 StartZ=0 EndX=882 EndY=206 EndZ=0
    g17: LineSegment StartX=882 StartY=206 StartZ=0 EndX=882 EndY=-388 EndZ=0
    g18: LineSegment StartX=882 StartY=-388 StartZ=0 EndX=41 EndY=-388 EndZ=0
    g19: LineSegment StartX=41 StartY=-388 StartZ=0 EndX=41 EndY=206 EndZ=0
    g20: LineSegment StartX=41 StartY=-388 StartZ=0 EndX=882 EndY=-388 EndZ=0
    g21: LineSegment StartX=882 StartY=-388 StartZ=0 EndX=882 EndY=-982 EndZ=0
    g22: LineSegment StartX=882 StartY=-982 StartZ=0 EndX=41 EndY=-982 EndZ=0
    g23: LineSegment StartX=41 StartY=-982 StartZ=0 EndX=41 EndY=-388 EndZ=0
  constraints (67):
    c: Coincident(g0,g1)
    c: Coincident(g1,g2)
    c: Coincident(g2,g3)
    c: Coincident(g3,g0)
    c: Horizontal(g0)
    c: Horizontal(g2)
    c: Vertical(g1)
    c: Vertical(g3)
    c: PointOnObject(g-3,g0)
    c: PointOnObject(g-4,g3)
    c: DistanceX(g0,g0) = 841
    c: DistanceY(g3,g3) = 594
    c: Coincident(g4,g5)
    c: Coincident(g5,g6)
    c: Coincident(g6,g7)
    c: Coincident(g7,g4)
    c: Horizontal(g4)
    c: Horizontal(g6)
    c: Vertical(g5)
    c: Vertical(g7)
    c: Coincident(g4,g2)
    c: Coincident(g8,g9)
    c: Coincident(g9,g10)
    c: Coincident(g10,g11)
    c: Coincident(g11,g8)
    c: Horizontal(g8)
    c: Horizontal(g10)
    c: Vertical(g9)
    c: Vertical(g11)
    c: Coincident(g8,g6)
    c: Coincident(g12,g13)
    c: Coincident(g13,g14)
    c: Coincident(g14,g15)
    c: Coincident(g15,g12)
    c: Horizontal(g12)
    c: Horizontal(g14)
    c: Vertical(g13)
    c: Vertical(g15)
    c: Coincident(g12,g0)
    c: Coincident(g16,g17)
    c: Coincident(g17,g18)
    c: Coincident(g18,g19)
    c: Coincident(g19,g16)
    c: Horizontal(g16)
    c: Horizontal(g18)
    c: Vertical(g17)
    c: Vertical(g19)
    c: Coincident(g16,g4)
    c: Equal(g7,g3)
    c: Equal(g6,g2)
    c: Equal(g13,g1)
    c: Equal(g0,g12)
    c: Equal(g18,g14)
    c: Equal(g17,g13)
    c: Equal(g9,g5)
    c: Equal(g10,g6)
    c: Coincident(g20,g21)
    c: Coincident(g21,g22)
    c: Coincident(g22,g23)
    c: Coincident(g23,g20)
    c: Horizontal(g20)
    c: Horizontal(g22)
    c: Vertical(g21)
    c: Vertical(g23)
    c: Coincident(g20,g5)
    c: Equal(g22,g10)
    c: Equal(g21,g17)
FEATURE [PartDesign::Body] Body  label="SketchMasters"
  Group = -> [Sketch,Sketch001,Sketch002,Sketch003,Sketch004,Sketch005]
  Origin = -> Origin001
FEATURE [App::Part] Part
  Group = -> [Body]
  Origin = -> Origin
FEATURE [TechDraw::DrawViewPart] View007
  CoarseView = false
  Direction = (0.577,-0.577,0.577)
  Focus = 100
  HardHidden = false
  IsoCount = 0
  IsoHidden = false
  IsoVisible = false
  LockPosition = false
  Perspective = false
  Rotation = 0
  Scale = 0.1
  ScaleType = 0
  SeamHidden = false
  SeamVisible = true
  SmoothHidden = false
  SmoothVisible = true
  Source = -> [Part011]
  X = 135.676
  XDirection = (0.707,0.707,0)
  Y = 110.168
FEATURE [TechDraw::DrawViewPart] View
  CoarseView = false
  Direction = (0,0,1)
  Focus = 100
  HardHidden = false
  IsoCount = 0
  IsoHidden = false
  IsoVisible = false
  LockPosition = false
  Perspective = false
  Rotation = 0
  Scale = 0.1
  ScaleType = 2
  SeamHidden = false
  SeamVisible = true
  SmoothHidden = false
  SmoothVisible = true
  Source = -> [Part011]
  X = 137.817
  XDirection = (1,0,0)
  Y = 112.872
FEATURE [TechDraw::DrawViewDimension] Dimension
  AngleOverride = false
  Arbitrary = false
  ArbitraryTolerances = false
  EqualTolerance = true
  ExtensionAngle = 0
  FormatSpec = %.2f
  FormatSpecOverTolerance = %+.2f
  FormatSpecUnderTolerance = %+.2f
  Inverted = false
  LineAngle = 0
  LockPosition = false
  MeasureType = 1
  OverTolerance = 0
  References2D = -> [View]
  Rotation = 0
  ScaleType = 0
  TheoreticalExact = false
  Type = 1
  UnderTolerance = 0
  X = -0.873752
  Y = 87.4562
FEATURE [TechDraw::DrawViewDimension] Dimension032
  AngleOverride = false
  Arbitrary = false
  ArbitraryTolerances = false
  EqualTolerance = true
  ExtensionAngle = 0
  FormatSpec = %.2f
  FormatSpecOverTolerance = %+.2f
  FormatSpecUnderTolerance = %+.2f
  Inverted = false
  LineAngle = 0
  LockPosition = false
  MeasureType = 1
  OverTolerance = 0
  References2D = -> [View]
  Rotation = 0
  ScaleType = 0
  TheoreticalExact = false
  Type = 2
  UnderTolerance = 0
  X = -88.1074
  Y = 3.7573
FEATURE [TechDraw::DrawViewDimension] Dimension033
  AngleOverride = false
  Arbitrary = false
  ArbitraryTolerances = false
  EqualTolerance = true
  ExtensionAngle = 0
  FormatSpec = %.2f
  FormatSpecOverTolerance = %+.2f
  FormatSpecUnderTolerance = %+.2f
  Inverted = false
  LineAngle = 0
  LockPosition = false
  MeasureType = 1
  OverTolerance = 0
  References2D = -> [View]
  Rotation = 0
  ScaleType = 0
  TheoreticalExact = false
  Type = 1
  UnderTolerance = 0
  X = 46.018
  Y = -2.80639
FEATURE [TechDraw::DrawViewDimension] Dimension044
  AngleOverride = false
  Arbitrary = false
  ArbitraryTolerances = false
  EqualTolerance = true
  ExtensionAngle = 0
  FormatSpec = %.2f
  FormatSpecOverTolerance = %+.2f
  FormatSpecUnderTolerance = %+.2f
  Inverted = false
  LineAngle = 0
  LockPosition = false
  MeasureType = 1
  OverTolerance = 0
  References2D = -> [View003]
  Rotation = 0
  ScaleType = 0
  TheoreticalExact = false
  Type = 1
  UnderTolerance = 0
  X = 4.69663
  Y = 35.1987
FEATURE [TechDraw::DrawHatch] Hatch008  label="Hatch008F0"
  HatchPattern = /Applications/FreeCAD.app/Contents/Resources/share/Mod/TechDraw/Patterns/simple.svg
  Source = -> View002 [Face0]
FEATURE [TechDraw::DrawHatch] Hatch009  label="Hatch009F0"
  HatchPattern = /Applications/FreeCAD.app/Contents/Resources/share/Mod/TechDraw/Patterns/simple.svg
  Source = -> View003 [Face0]
FEATURE [TechDraw::DrawHatch] Hatch010  label="Hatch010F0"
  HatchPattern = /Applications/FreeCAD.app/Contents/Resources/share/Mod/TechDraw/Patterns/simple.svg
  Source = -> View005 [Face0]
FEATURE [TechDraw::DrawHatch] Hatch011  label="Hatch011F0"
  HatchPattern = /Applications/FreeCAD.app/Contents/Resources/share/Mod/TechDraw/Patterns/simple.svg
  Source = -> View004 [Face0]
FEATURE [Spreadsheet::Sheet] Spreadsheet001  label="DrawingSheet"
  cells = A1=WH; B1=Wall Height; C1=210; A2=WT; B2=Wall Thickness; C2=10; A3=TL; B3=Tab Length; C3=40
FEATURE [TechDraw::DrawViewDimension] Dimension045
  AngleOverride = false
  Arbitrary = false
  ArbitraryTolerances = false
  EqualTolerance = true
  ExtensionAngle = 0
  FormatSpec = %.2f
  FormatSpecOverTolerance = %+.2f
  FormatSpecUnderTolerance = %+.2f
  Inverted = false
  LineAngle = 0
  LockPosition = false
  MeasureType = 1
  OverTolerance = 0
  References2D = -> [View005]
  Rotation = 0
  ScaleType = 0
  TheoreticalExact = false
  Type = 1
  UnderTolerance = 0
  X = -0.345467
  Y = 34.2957
FEATURE [TechDraw::DrawPage] Page002  label="ViewOfParts"
  KeepUpdated = true
  NextBalloonIndex = 1
  ProjectionType = 0
  Template = -> Template002
  Views = -> [View002,View003,View004,Annotation010,Annotation011,Dimension008,Dimension009,Dimension010,Dimension011,Dimension012,Annotation012,Dimension017,View005,Annotation013,Dimension044,Dimension045]
FEATURE [TechDraw::DrawLeaderLine] LeaderLine
  AutoHorizontal = false
  EndSymbol = 0
  LeaderParent = -> View007
  LockPosition = true
  Rotation = 0
  Scalable = false
  Scale = 0.1
  ScaleType = 0
  StartSymbol = 7
  WayPoints = (2) [(0,0,0),(0,115.444,0)]
  X = 227.199
  Y = -199.597
FEATURE [TechDraw::DrawPage] Page  label="3DView"
  KeepUpdated = true
  NextBalloonIndex = 1
  ProjectionType = 0
  Scale = 0.1
  Template = -> Template
  Views = -> [View007,Annotation001,Annotation002,Annotation004,Annotation003,Annotation,Annotation005,Annotation006,Annotation007,Annotation008,Annotation009,LeaderLine]
FEATURE [TechDraw::DrawHatch] Hatch  label="HatchF1"
  HatchPattern = /Applications/FreeCAD.app/Contents/Resources/share/Mod/TechDraw/Patterns/simple.svg
  Source = -> View [Face1]
FEATURE [TechDraw::DrawViewDimension] Dimension046
  AngleOverride = false
  Arbitrary = false
  ArbitraryTolerances = false
  EqualTolerance = true
  ExtensionAngle = 0
  FormatSpec = %.2f
  FormatSpecOverTolerance = %+.2f
  FormatSpecUnderTolerance = %+.2f
  Inverted = false
  LineAngle = 0
  LockPosition = false
  MeasureType = 1
  OverTolerance = 0
  References2D = -> [View]
  Rotation = 0
  ScaleType = 0
  TheoreticalExact = false
  Type = 2
  UnderTolerance = 0
  X = 8.38972
  Y = -52.0157
FEATURE [TechDraw::DrawPage] Page001  label="TopView"
  KeepUpdated = true
  NextBalloonIndex = 1
  ProjectionType = 0
  Template = -> Template001
  Views = -> [View,Dimension,Dimension032,Dimension033,Dimension046]
